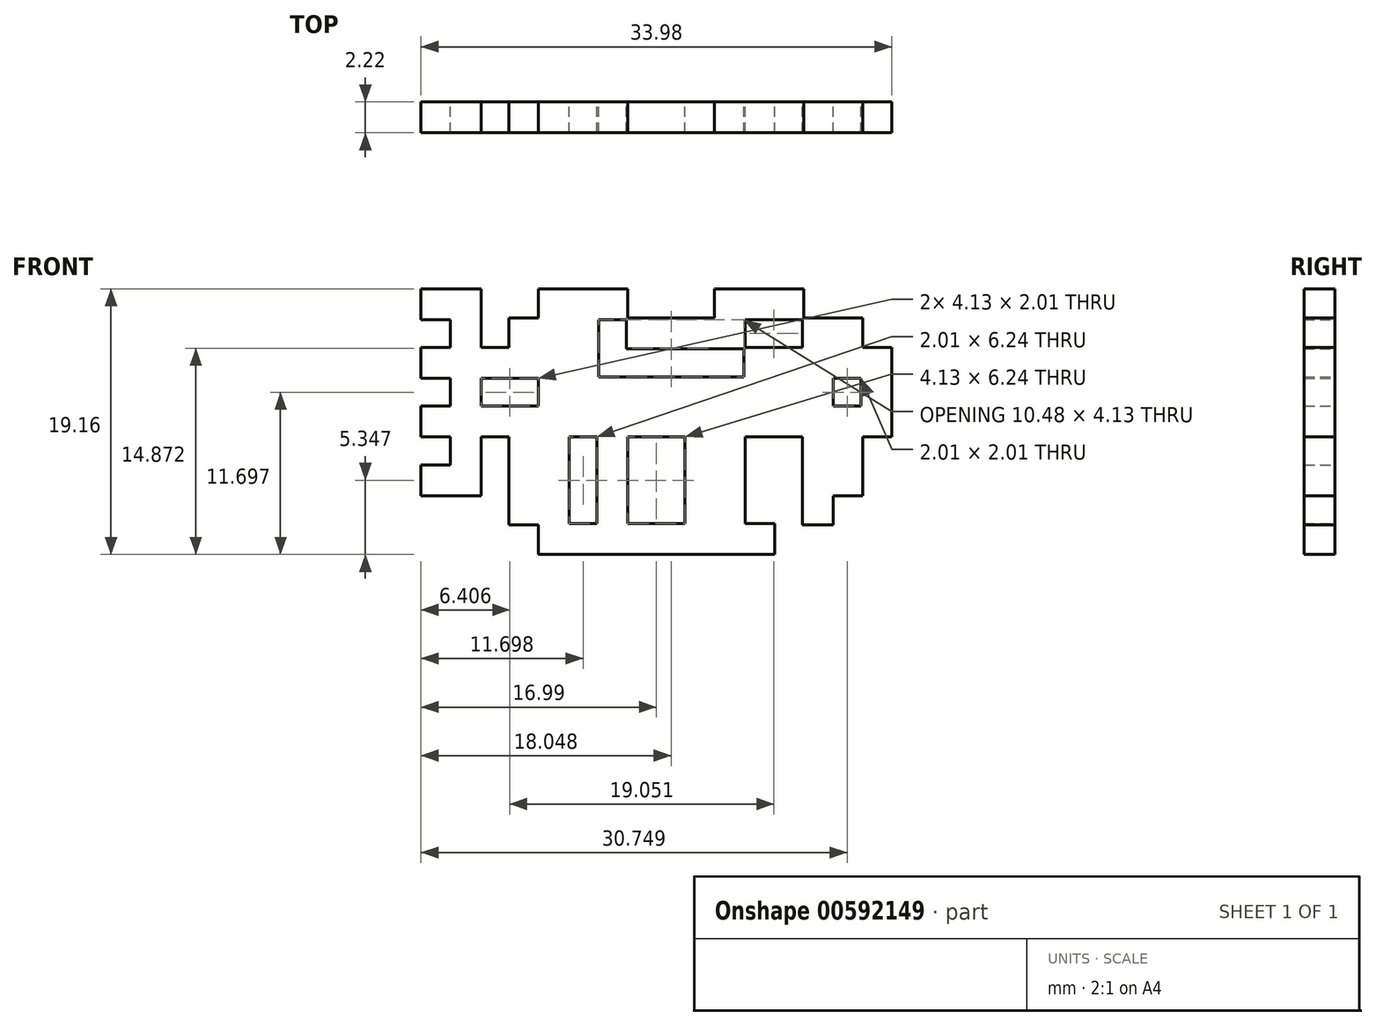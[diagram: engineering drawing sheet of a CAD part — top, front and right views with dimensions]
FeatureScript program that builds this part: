
annotation { "Feature Type Name" : "Feature", "Feature Type Description" : "" }
export const myFeature = defineFeature(function(context is Context, id is Id, definition is map)
    precondition{}
    {
        {
            var Q0;
            Q0=qCreatedBy(makeId("Front.planeOp"),FACE);
            var sketch = newSketch(context, id + "F0", { "sketchPlane" : qUnion([Q0])});
            skLineSegment(sketch, "E0", {"start": v(14.87, 5.34) * mm, "end": v(14.87, 7.46) * mm});
            skLineSegment(sketch, "E1", {"start": v(14.87, 7.46) * mm, "end": v(10.64, 7.46) * mm});
            skLineSegment(sketch, "E2", {"start": v(10.64, 7.46) * mm, "end": v(10.64, 9.58) * mm});
            skLineSegment(sketch, "E3", {"start": v(10.64, 9.58) * mm, "end": v(4.18, 9.58) * mm});
            skLineSegment(sketch, "E4", {"start": v(4.18, 9.58) * mm, "end": v(4.18, 7.46) * mm});
            skLineSegment(sketch, "E5", {"start": v(4.18, 7.46) * mm, "end": v(-2.06, 7.46) * mm});
            skLineSegment(sketch, "E6", {"start": v(-2.06, 7.46) * mm, "end": v(-2.06, 9.58) * mm});
            skLineSegment(sketch, "E7", {"start": v(-2.06, 9.58) * mm, "end": v(-8.52, 9.58) * mm});
            skLineSegment(sketch, "E8", {"start": v(-8.52, 9.58) * mm, "end": v(-8.52, 7.46) * mm});
            skLineSegment(sketch, "E9", {"start": v(-8.52, 7.46) * mm, "end": v(-10.64, 7.46) * mm});
            skLineSegment(sketch, "E10", {"start": v(-10.64, 7.46) * mm, "end": v(-10.64, 5.34) * mm});
            skLineSegment(sketch, "E11", {"start": v(-10.64, 5.34) * mm, "end": v(-12.65, 5.34) * mm});
            skLineSegment(sketch, "E12", {"start": v(-12.65, 5.34) * mm, "end": v(-12.65, 9.58) * mm});
            skLineSegment(sketch, "E13", {"start": v(-12.65, 9.58) * mm, "end": v(-16.99, 9.58) * mm});
            skLineSegment(sketch, "E14", {"start": v(-16.99, 9.58) * mm, "end": v(-16.99, 7.36) * mm});
            skLineSegment(sketch, "E15", {"start": v(-16.99, 7.36) * mm, "end": v(-14.87, 7.36) * mm});
            skLineSegment(sketch, "E16", {"start": v(-14.87, 7.36) * mm, "end": v(-14.87, 5.34) * mm});
            skLineSegment(sketch, "E17", {"start": v(-14.87, 5.34) * mm, "end": v(-16.99, 5.34) * mm});
            skLineSegment(sketch, "E18", {"start": v(-16.99, 5.34) * mm, "end": v(-16.99, 3.12) * mm});
            skLineSegment(sketch, "E19", {"start": v(-16.99, 3.12) * mm, "end": v(-14.87, 3.12) * mm});
            skLineSegment(sketch, "E20", {"start": v(-14.87, 3.12) * mm, "end": v(-14.87, 1.11) * mm});
            skLineSegment(sketch, "E21", {"start": v(-14.87, 1.11) * mm, "end": v(-16.99, 1.11) * mm});
            skLineSegment(sketch, "E22", {"start": v(-16.99, 1.11) * mm, "end": v(-16.99, -1.11) * mm});
            skLineSegment(sketch, "E23", {"start": v(-16.99, -1.11) * mm, "end": v(-14.87, -1.11) * mm});
            skLineSegment(sketch, "E24", {"start": v(-14.87, -1.11) * mm, "end": v(-14.87, -3.12) * mm});
            skLineSegment(sketch, "E25", {"start": v(-14.87, -3.12) * mm, "end": v(-16.99, -3.12) * mm});
            skLineSegment(sketch, "E26", {"start": v(-16.99, -3.12) * mm, "end": v(-16.99, -5.34) * mm});
            skLineSegment(sketch, "E27", {"start": v(-16.99, -5.34) * mm, "end": v(-12.65, -5.34) * mm});
            skLineSegment(sketch, "E28", {"start": v(-12.65, -5.34) * mm, "end": v(-12.65, -1.11) * mm});
            skLineSegment(sketch, "E29", {"start": v(-12.65, -1.11) * mm, "end": v(-10.64, -1.11) * mm});
            skLineSegment(sketch, "E30", {"start": v(-10.64, -1.11) * mm, "end": v(-10.64, -7.46) * mm});
            skLineSegment(sketch, "E31", {"start": v(-10.64, -7.46) * mm, "end": v(-8.52, -7.46) * mm});
            skLineSegment(sketch, "E32", {"start": v(-8.52, -7.46) * mm, "end": v(-8.52, -9.58) * mm});
            skLineSegment(sketch, "E33", {"start": v(-8.52, -9.58) * mm, "end": v(8.52, -9.58) * mm});
            skLineSegment(sketch, "E34", {"start": v(8.52, -9.58) * mm, "end": v(8.52, -7.36) * mm});
            skLineSegment(sketch, "E35", {"start": v(8.52, -7.36) * mm, "end": v(6.4, -7.36) * mm});
            skLineSegment(sketch, "E36", {"start": v(6.4, -7.36) * mm, "end": v(6.4, -1.11) * mm});
            skLineSegment(sketch, "E37", {"start": v(6.4, -1.11) * mm, "end": v(10.53, -1.11) * mm});
            skLineSegment(sketch, "E38", {"start": v(10.53, -1.11) * mm, "end": v(10.53, -7.46) * mm});
            skLineSegment(sketch, "E39", {"start": v(10.53, -7.46) * mm, "end": v(12.75, -7.46) * mm});
            skLineSegment(sketch, "E40", {"start": v(12.75, -7.46) * mm, "end": v(12.75, -5.34) * mm});
            skLineSegment(sketch, "E41", {"start": v(12.75, -5.34) * mm, "end": v(14.87, -5.34) * mm});
            skLineSegment(sketch, "E42", {"start": v(14.87, -5.34) * mm, "end": v(14.87, -1.11) * mm});
            skLineSegment(sketch, "E43", {"start": v(14.87, -1.11) * mm, "end": v(16.99, -1.11) * mm});
            skLineSegment(sketch, "E44", {"start": v(16.99, -1.11) * mm, "end": v(16.99, 5.34) * mm});
            skLineSegment(sketch, "E45", {"start": v(16.99, 5.34) * mm, "end": v(14.87, 5.34) * mm});
            skLineSegment(sketch, "E46", {"start": v(-8.52, 1.11) * mm, "end": v(-12.65, 1.11) * mm});
            skLineSegment(sketch, "E47", {"start": v(-12.65, 1.11) * mm, "end": v(-12.65, 3.12) * mm});
            skLineSegment(sketch, "E48", {"start": v(-12.65, 3.12) * mm, "end": v(-8.52, 3.12) * mm});
            skLineSegment(sketch, "E49", {"start": v(-8.52, 3.12) * mm, "end": v(-8.52, 1.11) * mm});
            skLineSegment(sketch, "E50", {"start": v(-4.29, -7.36) * mm, "end": v(-6.3, -7.36) * mm});
            skLineSegment(sketch, "E51", {"start": v(-6.3, -7.36) * mm, "end": v(-6.3, -1.11) * mm});
            skLineSegment(sketch, "E52", {"start": v(-6.3, -1.11) * mm, "end": v(-4.29, -1.11) * mm});
            skLineSegment(sketch, "E53", {"start": v(-4.29, -1.11) * mm, "end": v(-4.29, -7.36) * mm});
            skLineSegment(sketch, "E54", {"start": v(2.06, -7.36) * mm, "end": v(-2.06, -7.36) * mm});
            skLineSegment(sketch, "E55", {"start": v(-2.06, -7.36) * mm, "end": v(-2.06, -1.11) * mm});
            skLineSegment(sketch, "E56", {"start": v(-2.06, -1.11) * mm, "end": v(2.06, -1.11) * mm});
            skLineSegment(sketch, "E57", {"start": v(2.06, -1.11) * mm, "end": v(2.06, -7.36) * mm});
            skLineSegment(sketch, "E58", {"start": v(6.3, 3.23) * mm, "end": v(-4.18, 3.23) * mm});
            skLineSegment(sketch, "E59", {"start": v(-4.18, 3.23) * mm, "end": v(-4.18, 7.36) * mm});
            skLineSegment(sketch, "E60", {"start": v(-4.18, 7.36) * mm, "end": v(-2.17, 7.36) * mm});
            skLineSegment(sketch, "E61", {"start": v(-2.17, 7.36) * mm, "end": v(-2.17, 5.24) * mm});
            skLineSegment(sketch, "E62", {"start": v(-2.17, 5.24) * mm, "end": v(6.3, 5.24) * mm});
            skLineSegment(sketch, "E63", {"start": v(6.3, 5.24) * mm, "end": v(6.3, 3.23) * mm});
            skLineSegment(sketch, "E64", {"start": v(10.53, 5.34) * mm, "end": v(6.4, 5.34) * mm});
            skLineSegment(sketch, "E65", {"start": v(6.4, 5.34) * mm, "end": v(6.4, 7.36) * mm});
            skLineSegment(sketch, "E66", {"start": v(6.4, 7.36) * mm, "end": v(10.53, 7.36) * mm});
            skLineSegment(sketch, "E67", {"start": v(10.53, 7.36) * mm, "end": v(10.53, 5.34) * mm});
            skLineSegment(sketch, "E68", {"start": v(14.76, 1.11) * mm, "end": v(12.75, 1.11) * mm});
            skLineSegment(sketch, "E69", {"start": v(12.75, 1.11) * mm, "end": v(12.75, 3.12) * mm});
            skLineSegment(sketch, "E70", {"start": v(12.75, 3.12) * mm, "end": v(14.76, 3.12) * mm});
            skLineSegment(sketch, "E71", {"start": v(14.76, 3.12) * mm, "end": v(14.76, 1.11) * mm});
            skSolve(sketch);
        }
        {
            var Q0;
            Q0 = qSketchRegion(id + "F0", true);
            extrude(context, id + "F1", {"entities" : qUnion([Q0]), "depth" : 2.22 * mm, "offsetDistance" : 25 * mm});
        }
    });
